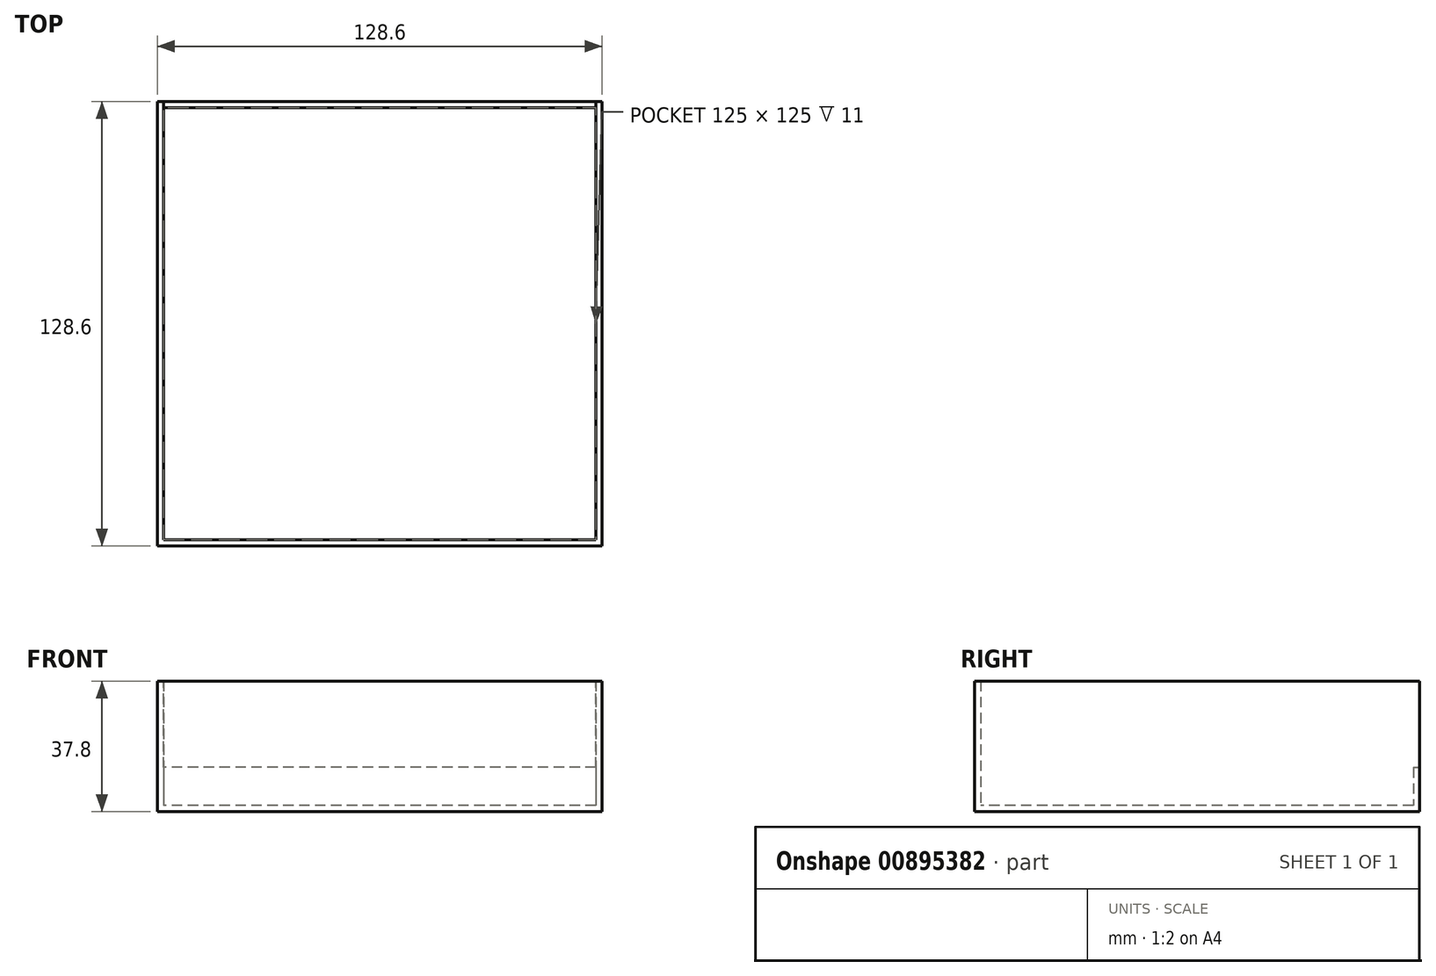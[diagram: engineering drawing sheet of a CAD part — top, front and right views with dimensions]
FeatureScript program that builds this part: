
annotation { "Feature Type Name" : "Feature", "Feature Type Description" : "" }
export const myFeature = defineFeature(function(context is Context, id is Id, definition is map)
    precondition{}
    {
        {
            assignVariable(context, id + "F0", {"name" : "hau", "anyValue" : 36});
        }
        {
            assignVariable(context, id + "F1", {"name" : "ep", "anyValue" : .9});
        }
        {
            var Q0;
            Q0=qCreatedBy(makeId("Top.planeOp"),FACE);
            var sketch = newSketch(context, id + "F2", { "sketchPlane" : qUnion([Q0])});
            skLineSegment(sketch, "E0.bottom", {"start": v(62.5, 62.5) * mm, "end": v(-62.5, 62.5) * mm});
            skLineSegment(sketch, "E0.top", {"start": v(62.5, -62.5) * mm, "end": v(-62.5, -62.5) * mm});
            skLineSegment(sketch, "E0.left", {"start": v(62.5, 62.5) * mm, "end": v(62.5, -62.5) * mm});
            skLineSegment(sketch, "E0.right", {"start": v(-62.5, 62.5) * mm, "end": v(-62.5, -62.5) * mm});
            skPoint(sketch, "E0.middle", {"position": v(0, 0) * mm});
            skLineSegment(sketch, "E1.0", {"start": v(64.3, 64.3) * mm, "end": v(-64.3, 64.3) * mm});
            skLineSegment(sketch, "E1.1", {"start": v(64.3, 64.3) * mm, "end": v(64.3, -64.3) * mm});
            skLineSegment(sketch, "E1.2", {"start": v(64.3, -64.3) * mm, "end": v(-64.3, -64.3) * mm});
            skLineSegment(sketch, "E1.3", {"start": v(-64.3, 64.3) * mm, "end": v(-64.3, -64.3) * mm});
            skSolve(sketch);
        }
        {
            var Q0;
            Q0=makeQuery(id+"F2.imprint","IMPRINT",FACE,{"disambiguationData":[TD([[makeQuery(id+"F2.imprint","IMPRINT",EDGE,{"derivedFrom":sQuery(id+"F2.wireOp",EDGE,"E0.bottom")}),-1.0]])]});
            extrude(context, id + "F3", {"entities" : qUnion([Q0]), "depth" : (getVariable(context, 'hau')) * mm, "offsetDistance" : 25 * mm});
        }
        {
            var Q0;
            Q0=makeQuery(id+"F2.imprint","IMPRINT",FACE,{"disambiguationData":[TD([[makeQuery(id+"F2.imprint","IMPRINT",EDGE,{"derivedFrom":sQuery(id+"F2.wireOp",EDGE,"E0.bottom")}),1.0]])]});
            var Q1;
            Q1=makeQuery(id+"F2.imprint","IMPRINT",FACE,{"disambiguationData":[TD([[makeQuery(id+"F2.imprint","IMPRINT",EDGE,{"derivedFrom":sQuery(id+"F2.wireOp",EDGE,"E0.bottom")}),-1.0]])]});
            extrude(context, id + "F4", {"entities" : qUnion([Q0, Q1]), "operationType" : NewBodyOperationType.ADD, "oppositeDirection" : true, "depth" : (2 * getVariable(context, 'ep')) * mm, "offsetDistance" : 25 * mm});
        }
        {
            var Q0;
            Q0=makeQuery(id+"F3.opExtrude","CAP_FACE",FACE,{"disambiguationData":[OSD([sQuery(id+"F2.wireOp",EDGE,"E0.bottom"),sQuery(id+"F2.wireOp",EDGE,"E0.top"),sQuery(id+"F2.wireOp",EDGE,"E0.left"),sQuery(id+"F2.wireOp",EDGE,"E0.right"),sQuery(id+"F2.wireOp",EDGE,"E1.0"),sQuery(id+"F2.wireOp",EDGE,"E1.1"),sQuery(id+"F2.wireOp",EDGE,"E1.2"),sQuery(id+"F2.wireOp",EDGE,"E1.3")])],"isStart":false});
            var sketch = newSketch(context, id + "F5", { "sketchPlane" : qUnion([Q0])});
            skLineSegment(sketch, "E2.bottom", {"start": v(62.5, 62.5) * mm, "end": v(-62.5, 62.5) * mm});
            skLineSegment(sketch, "E2.top", {"start": v(62.5, 64.3) * mm, "end": v(-62.5, 64.3) * mm});
            skLineSegment(sketch, "E2.left", {"start": v(62.5, 62.5) * mm, "end": v(62.5, 64.3) * mm});
            skLineSegment(sketch, "E2.right", {"start": v(-62.5, 62.5) * mm, "end": v(-62.5, 64.3) * mm});
            skSolve(sketch);
        }
        {
            var Q0;
            Q0 = qSketchRegion(id + "F5", true);
            extrude(context, id + "F6", {"entities" : qUnion([Q0]), "operationType" : NewBodyOperationType.REMOVE, "oppositeDirection" : true, "depth" : 25 * mm, "offsetDistance" : 25 * mm});
        }
    });
